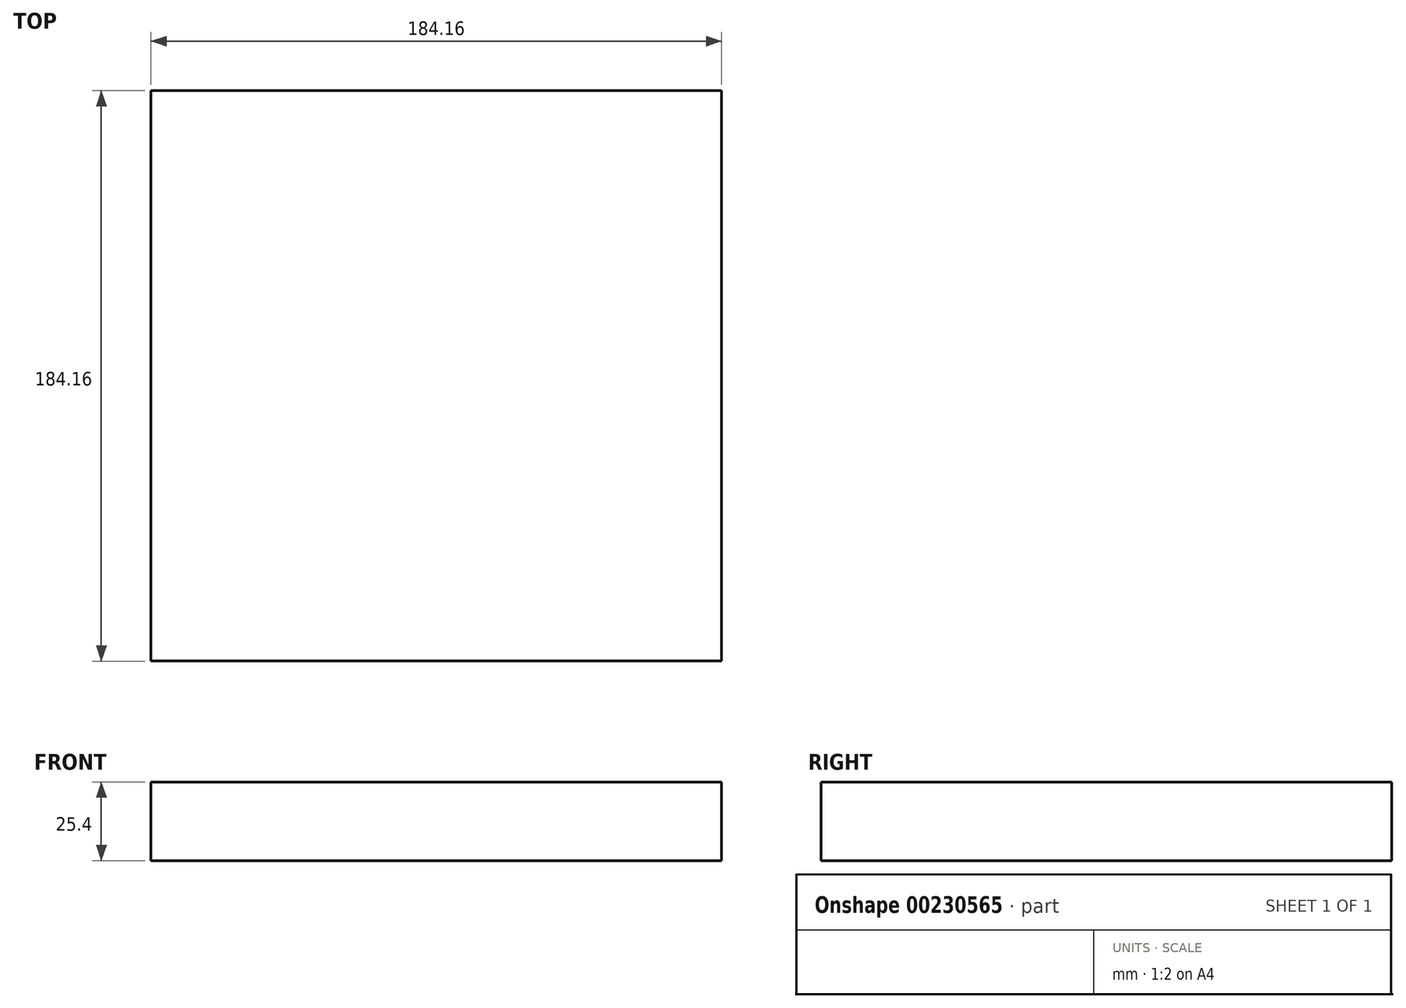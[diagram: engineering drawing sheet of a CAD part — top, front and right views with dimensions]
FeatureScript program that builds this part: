
annotation { "Feature Type Name" : "Feature", "Feature Type Description" : "" }
export const myFeature = defineFeature(function(context is Context, id is Id, definition is map)
    precondition{}
    {
        {
            var Q0;
            Q0=qCreatedBy(makeId("Top.planeOp"),FACE);
            var sketch = newSketch(context, id + "F0", { "sketchPlane" : qUnion([Q0])});
            skLineSegment(sketch, "E0.bottom", {"start": v(92.08, 92.08) * mm, "end": v(-92.08, 92.08) * mm});
            skLineSegment(sketch, "E0.top", {"start": v(92.07, -92.08) * mm, "end": v(-92.08, -92.08) * mm});
            skLineSegment(sketch, "E0.left", {"start": v(92.08, 92.08) * mm, "end": v(92.07, -92.08) * mm});
            skLineSegment(sketch, "E0.right", {"start": v(-92.08, 92.08) * mm, "end": v(-92.08, -92.08) * mm});
            skPoint(sketch, "E0.middle", {"position": v(0, 0) * mm});
            skSolve(sketch);
        }
        {
            var Q0;
            Q0 = qSketchRegion(id + "F0", true);
            extrude(context, id + "F1", {"entities" : qUnion([Q0]), "depth" : 25.4 * mm});
        }
    });
